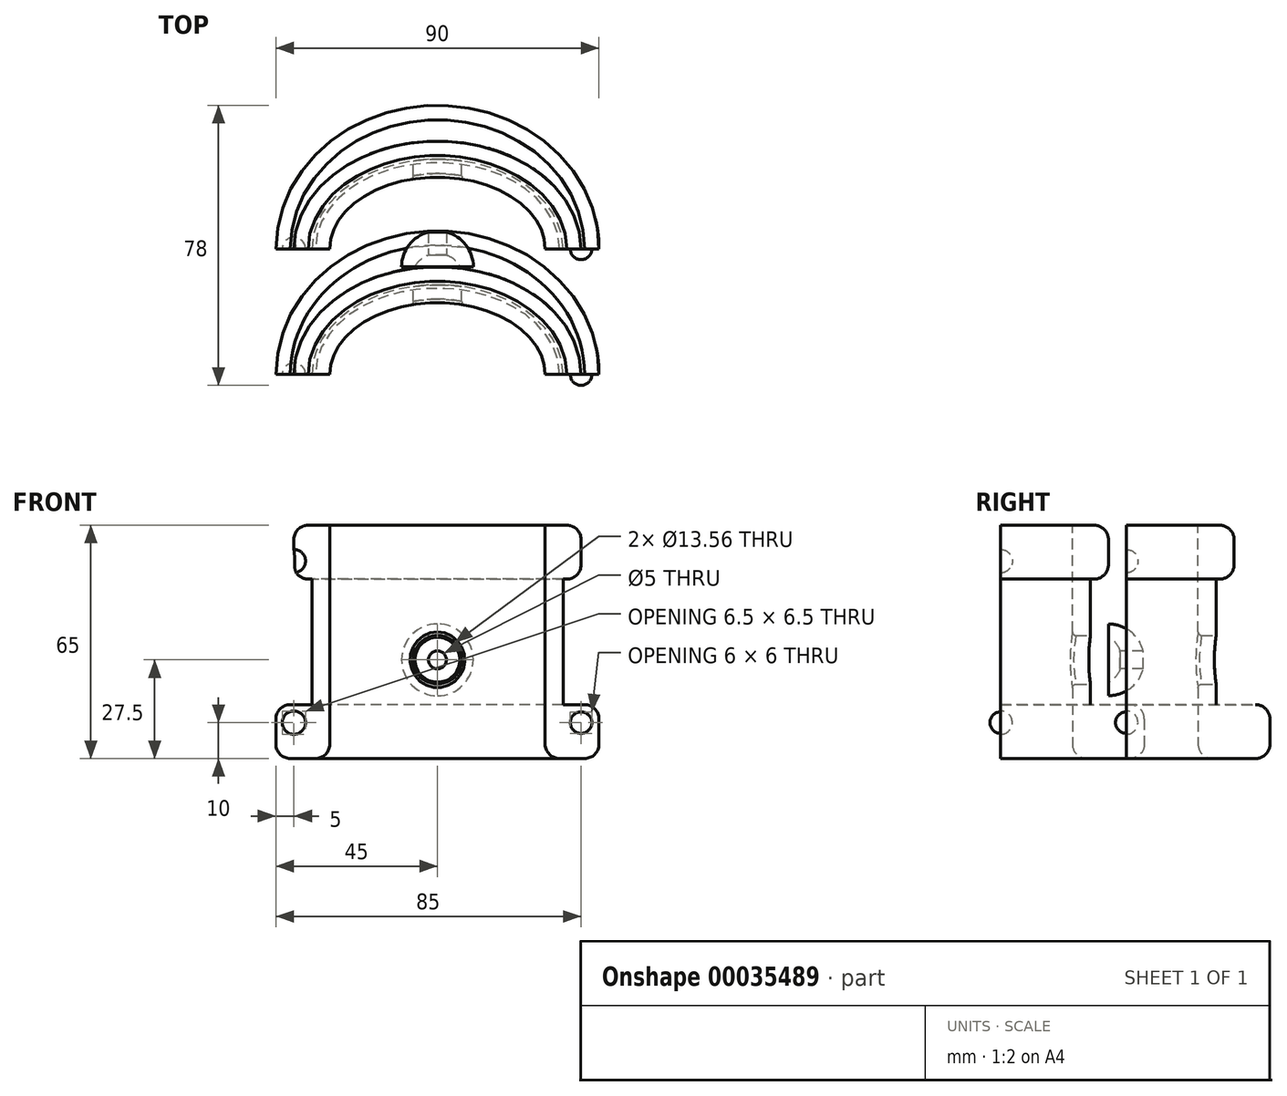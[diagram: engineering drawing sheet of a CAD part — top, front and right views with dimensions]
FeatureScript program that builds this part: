
annotation { "Feature Type Name" : "Feature", "Feature Type Description" : "" }
export const myFeature = defineFeature(function(context is Context, id is Id, definition is map)
    precondition{}
    {
        {
            var Q0;
            Q0=qCreatedBy(makeId("Top.planeOp"),FACE);
            var sketch = newSketch(context, id + "F0", { "sketchPlane" : qUnion([Q0])});
            skEllipse(sketch, "E0", {"center": v(0, 0) * mm, "majorRadius": 45 * mm, "minorRadius": 40 * mm, "majorAxis": v(1, 0)});
            skSolve(sketch);
        }
        {
            var Q0;
            Q0 = qSketchRegion(id + "F0", true);
            extrude(context, id + "F1", {"entities" : qUnion([Q0]), "depth" : 15 * mm});
        }
        {
            var Q0;
            Q0=makeQuery(id+"F1.opExtrude","CAP_FACE",FACE,{"disambiguationData":[OSD([sQuery(id+"F0.wireOp",EDGE,"E0")])],"isStart":false});
            var sketch = newSketch(context, id + "F2", { "sketchPlane" : qUnion([Q0])});
            skEllipse(sketch, "E1", {"center": v(0, 0) * mm, "majorRadius": 35 * mm, "minorRadius": 25 * mm, "majorAxis": v(1, 0)});
            skLineSegment(sketch, "E2", {"start": v(40, 0) * mm, "end": v(45, 0) * mm, "construction": true});
            skLineSegment(sketch, "E3", {"start": v(0, 35) * mm, "end": v(0, 40) * mm, "construction": true});
            skSolve(sketch);
        }
        {
            var Q0;
            Q0 = qSketchRegion(id + "F2", true);
            extrude(context, id + "F3", {"entities" : qUnion([Q0]), "operationType" : NewBodyOperationType.ADD, "depth" : 35 * mm});
        }
        {
            var Q0;
            Q0=makeQuery(id+"F3.opExtrude","CAP_FACE",FACE,{"disambiguationData":[OSD([sQuery(id+"F2.wireOp",EDGE,"E1")])],"isStart":false});
            var sketch = newSketch(context, id + "F4", { "sketchPlane" : qUnion([Q0])});
            skEllipse(sketch, "E4.0", {"center": v(0, 0) * mm, "majorRadius": 40 * mm, "minorRadius": 30 * mm, "majorAxis": v(1, 0)});
            skSolve(sketch);
        }
        {
            var Q0;
            Q0 = qSketchRegion(id + "F4", true);
            extrude(context, id + "F5", {"entities" : qUnion([Q0]), "operationType" : NewBodyOperationType.ADD, "depth" : 15 * mm});
        }
        {
            var Q0;
            Q0=qCreatedBy(makeId("Front.planeOp"),FACE);
            cPlane(context, id + "F6", {"entities" : qUnion([Q0]), "cplaneType" : CPlaneType.OFFSET, "offset" : 20 * mm, "width" : 150 * mm, "height" : 150 * mm});
        }
        {
            var Q0;
            Q0=qCreatedBy(id+"F6.planeOp",FACE);
            var sketch = newSketch(context, id + "F7", { "sketchPlane" : qUnion([Q0])});
            skLineSegment(sketch, "E5", {"start": v(0, 0) * mm, "end": v(0, 27.5) * mm, "construction": true});
            skLineSegment(sketch, "E6", {"start": v(0, 17.5) * mm, "end": v(0, 37.5) * mm});
            skArc(sketch, "E7", {"start": v(0, 17.5) * mm, "mid": v(10, 27.5) * mm, "end": v(0, 37.5) * mm});
            skSolve(sketch);
        }
        {
            var Q0;
            Q0 = qSketchRegion(id + "F7", true);
            var Q1;
            Q1=sQuery(id+"F7.wireOp",EDGE,"E6");
            revolve(context, id + "F8", {"operationType" : NewBodyOperationType.ADD, "entities" : qUnion([Q0]), "axis" : qUnion([Q1]), "revolveType" : RevolveType.ONE_DIRECTION, "oppositeDirection" : true, "angle" : 180 * degree});
        }
        {
            var Q0;
            Q0=qCreatedBy(makeId("Front.planeOp"),FACE);
            cPlane(context, id + "F9", {"entities" : qUnion([Q0]), "cplaneType" : CPlaneType.OFFSET, "offset" : 30 * mm, "oppositeDirection" : true, "width" : 150 * mm, "height" : 150 * mm});
        }
        {
            var Q0;
            Q0=qCreatedBy(id+"F9.planeOp",FACE);
            var sketch = newSketch(context, id + "F10", { "sketchPlane" : qUnion([Q0])});
            skArc(sketch, "E8.0", {"start": v(0, 17.5) * mm, "mid": v(10, 27.5) * mm, "end": v(0, 37.5) * mm});
            skLineSegment(sketch, "E9.0", {"start": v(0, 17.5) * mm, "end": v(0, 37.5) * mm});
            skSolve(sketch);
        }
        {
            var Q0;
            Q0 = qSketchRegion(id + "F10", true);
            var Q1;
            Q1=sQuery(id+"F10.wireOp",EDGE,"E9.0");
            revolve(context, id + "F11", {"operationType" : NewBodyOperationType.ADD, "entities" : qUnion([Q0]), "axis" : qUnion([Q1]), "revolveType" : RevolveType.ONE_DIRECTION, "angle" : 180 * degree});
        }
        {
            var Q0;
            Q0=makeQuery(id+"F5.opExtrude","CAP_FACE",FACE,{"disambiguationData":[OSD([sQuery(id+"F4.wireOp",EDGE,"E4.0")])],"isStart":false});
            var sketch = newSketch(context, id + "F12", { "sketchPlane" : qUnion([Q0])});
            skEllipse(sketch, "E10", {"center": v(0, 0) * mm, "majorRadius": 30 * mm, "minorRadius": 20 * mm, "majorAxis": v(-1, 0)});
            skLineSegment(sketch, "E11", {"start": v(-35, 0) * mm, "end": v(-45, 0) * mm, "construction": true});
            skLineSegment(sketch, "E12", {"start": v(0, -30) * mm, "end": v(0, -40) * mm, "construction": true});
            skSolve(sketch);
        }
        {
            var Q0;
            Q0 = qSketchRegion(id + "F12", true);
            extrude(context, id + "F13", {"entities" : qUnion([Q0]), "operationType" : NewBodyOperationType.REMOVE, "endBound" : BoundingType.THROUGH_ALL, "oppositeDirection" : true, "depth" : 25 * mm});
        }
        {
            var Q0;
            Q0=qCreatedBy(makeId("Front.planeOp"),FACE);
            var sketch = newSketch(context, id + "F14", { "sketchPlane" : qUnion([Q0])});
            skPoint(sketch, "E13.0", {"position": v(0, 27.5) * mm});
            skCircle(sketch, "E14", {"center": v(0, 27.5) * mm, "radius": 2.5 * mm});
            skSolve(sketch);
        }
        {
            var Q0;
            Q0 = qSketchRegion(id + "F14", true);
            extrude(context, id + "F15", {"entities" : qUnion([Q0]), "operationType" : NewBodyOperationType.REMOVE, "endBound" : BoundingType.THROUGH_ALL, "oppositeDirection" : true, "depth" : 25 * mm, "hasSecondDirection" : true, "secondDirectionBound" : SecondDirectionBoundingType.THROUGH_ALL, "secondDirectionOppositeDirection" : false, "secondDirectionDepth" : 25 * mm});
        }
        {
            var Q0;
            Q0=makeQuery(id+"F13.boolean.opBoolean","COPY",EDGE,{"derivedFrom":makeQuery(id+"F13.opExtrude","CAP_EDGE",EDGE,{"disambiguationData":[OSD([sQuery(id+"F12.wireOp",EDGE,"E10")])],"isStart":true})});
            var Q1;
            Q1=makeQuery(id+"F5.opExtrude","CAP_EDGE",EDGE,{"disambiguationData":[OSD([sQuery(id+"F4.wireOp",EDGE,"E4.0")])],"isStart":false});
            var Q2;
            Q2=makeQuery(id+"F1.opExtrude","CAP_EDGE",EDGE,{"disambiguationData":[OSD([sQuery(id+"F0.wireOp",EDGE,"E0")])],"isStart":false});
            var Q3;
            Q3=makeQuery(id+"F1.opExtrude","CAP_EDGE",EDGE,{"disambiguationData":[OSD([sQuery(id+"F0.wireOp",EDGE,"E0")])],"isStart":true});
            var Q4;
            Q4=makeQuery(id+"F13.boolean.opBoolean","INTERSECT",EDGE,{"derivedFrom":[makeQuery(id+"F1.opExtrude","CAP_FACE",FACE,{"disambiguationData":[OSD([sQuery(id+"F0.wireOp",EDGE,"E0")])],"isStart":true}),makeQuery(id+"F13.opExtrude","SWEPT_FACE",FACE,{"disambiguationData":[OSD([sQuery(id+"F12.wireOp",EDGE,"E10")])]})]});
            var Q5;
            Q5=makeQuery(id+"F5.opExtrude","CAP_EDGE",EDGE,{"disambiguationData":[OSD([sQuery(id+"F4.wireOp",EDGE,"E4.0")])],"isStart":true});
            fillet(context, id + "F16", {"entities" : qUnion([Q0, Q1, Q2, Q3, Q4, Q5]), "radius" : 4 * mm, "tangentPropagation" : true, "allowEdgeOverflow" : false});
        }
        {
            var Q0;
            Q0=qCreatedBy(makeId("Right.planeOp"),FACE);
            var sketch = newSketch(context, id + "F17", { "sketchPlane" : qUnion([Q0])});
            skPoint(sketch, "E15.0", {"position": v(-20, 27.5) * mm});
            skLineSegment(sketch, "E16", {"start": v(0, 0) * mm, "end": v(0, 27.5) * mm, "construction": true});
            skLineSegment(sketch, "E17.rect.top", {"start": v(-27.5, 20.72) * mm, "end": v(27.5, 20.72) * mm});
            skPoint(sketch, "E17.rect.middle", {"position": v(0, 27.5) * mm});
            skLineSegment(sketch, "E18", {"start": v(-33.5, 27.5) * mm, "end": v(33.5, 27.5) * mm});
            skArc(sketch, "E19", {"start": v(-33.5, 27.5) * mm, "mid": v(-32.03, 22.76) * mm, "end": v(-27.5, 20.72) * mm});
            skArc(sketch, "E20.MirrorCS", {"start": v(33.5, 27.5) * mm, "mid": v(32.03, 22.76) * mm, "end": v(27.5, 20.72) * mm});
            skSolve(sketch);
        }
        {
            var Q0;
            Q0 = qSketchRegion(id + "F17", true);
            var Q1;
            Q1=sQuery(id+"F17.wireOp",EDGE,"E18");
            revolve(context, id + "F18", {"operationType" : NewBodyOperationType.REMOVE, "entities" : qUnion([Q0]), "axis" : qUnion([Q1]), "revolveType" : RevolveType.FULL, "oppositeDirection" : true});
        }
        {
            var Q0;
            Q0=makeQuery(id+"F3.opExtrude","CAP_EDGE",EDGE,{"disambiguationData":[OSD([sQuery(id+"F2.wireOp",EDGE,"E1")])],"isStart":true});
            var Q1;
            Q1=makeQuery(id+"F3.opExtrude","CAP_EDGE",EDGE,{"disambiguationData":[OSD([sQuery(id+"F2.wireOp",EDGE,"E1")])],"isStart":false});
            var Q2;
            Q2=makeQuery(id+"F18.boolean.opBoolean","INTERSECT",EDGE,{"disambiguationData":[OD(2.0)],"derivedFrom":[makeQuery(id+"F13.boolean.opBoolean","COPY",FACE,{"derivedFrom":makeQuery(id+"F13.opExtrude","SWEPT_FACE",FACE,{"disambiguationData":[OSD([sQuery(id+"F12.wireOp",EDGE,"E10")])]})}),makeQuery(id+"F18.opRevolve","SWEPT_FACE",FACE,{"disambiguationData":[OSD([sQuery(id+"F17.wireOp",EDGE,"E17.rect.top")])]})]});
            var Q3;
            Q3=makeQuery(id+"F18.boolean.opBoolean","INTERSECT",EDGE,{"disambiguationData":[OD(0.0)],"derivedFrom":[makeQuery(id+"F13.boolean.opBoolean","COPY",FACE,{"derivedFrom":makeQuery(id+"F13.opExtrude","SWEPT_FACE",FACE,{"disambiguationData":[OSD([sQuery(id+"F12.wireOp",EDGE,"E10")])]})}),makeQuery(id+"F18.opRevolve","SWEPT_FACE",FACE,{"disambiguationData":[OSD([sQuery(id+"F17.wireOp",EDGE,"E17.rect.top")])]})]});
            fillet(context, id + "F19", {"entities" : qUnion([Q0, Q1, Q2, Q3]), "radius" : 1 * mm, "tangentPropagation" : true, "allowEdgeOverflow" : false});
        }
        {
            var Q0;
            Q0=qCreatedBy(makeId("Top.planeOp"),FACE);
            var sketch = newSketch(context, id + "F20", { "sketchPlane" : qUnion([Q0])});
            skLineSegment(sketch, "E21", {"start": v(50, 0) * mm, "end": v(-50, 0) * mm, "construction": true});
            skLineSegment(sketch, "E22.bottom", {"start": v(50, 0) * mm, "end": v(-50, 0) * mm});
            skLineSegment(sketch, "E22.top", {"start": v(50, -40) * mm, "end": v(-50, -40) * mm});
            skLineSegment(sketch, "E22.left", {"start": v(50, 0) * mm, "end": v(50, -40) * mm});
            skLineSegment(sketch, "E22.right", {"start": v(-50, 0) * mm, "end": v(-50, -40) * mm});
            skSolve(sketch);
        }
        {
            var Q0;
            Q0 = qSketchRegion(id + "F20", true);
            extrude(context, id + "F21", {"entities" : qUnion([Q0]), "operationType" : NewBodyOperationType.REMOVE, "endBound" : BoundingType.THROUGH_ALL, "depth" : 25 * mm});
        }
        {
            var Q0;
            Q0=makeQuery(id+"F21.boolean.opBoolean","COPY",FACE,{"disambiguationData":[OD(1.0)],"derivedFrom":makeQuery(id+"F21.opExtrude","SWEPT_FACE",FACE,{"disambiguationData":[OSD([sQuery(id+"F20.wireOp",EDGE,"E22.bottom")])]})});
            var sketch = newSketch(context, id + "F22", { "sketchPlane" : qUnion([Q0])});
            skLineSegment(sketch, "E23", {"start": v(0, 0) * mm, "end": v(0, 10) * mm, "construction": true});
            skLineSegment(sketch, "E24", {"start": v(0, 10) * mm, "end": v(40, 10) * mm, "construction": true});
            skLineSegment(sketch, "E25", {"start": v(40, 7) * mm, "end": v(40, 13) * mm});
            skArc(sketch, "E26", {"start": v(40, 7) * mm, "mid": v(43, 10) * mm, "end": v(40, 13) * mm});
            skLineSegment(sketch, "E27", {"start": v(35, 32.5) * mm, "end": v(18.77, 32.5) * mm, "construction": true});
            skArc(sketch, "E28.MirrorCS", {"start": v(40, 58) * mm, "mid": v(43, 55) * mm, "end": v(40, 52) * mm});
            skLineSegment(sketch, "E29.MirrorCS", {"start": v(40, 58) * mm, "end": v(40, 52) * mm});
            skSolve(sketch);
        }
        {
            var Q0;
            Q0=makeQuery(id+"F22.imprint","IMPRINT",FACE,{"disambiguationData":[TD([[makeQuery(id+"F22.imprint","IMPRINT",EDGE,{"derivedFrom":sQuery(id+"F22.wireOp",EDGE,"E25")}),-1.0]])]});
            var Q1;
            Q1=makeQuery(id+"F22.imprint","IMPRINT",FACE,{"disambiguationData":[TD([[makeQuery(id+"F22.imprint","IMPRINT",EDGE,{"derivedFrom":sQuery(id+"F22.wireOp",EDGE,"E28.MirrorCS")}),-1.0]])]});
            var Q2;
            Q2=sQuery(id+"F22.wireOp",EDGE,"E25");
            revolve(context, id + "F23", {"operationType" : NewBodyOperationType.ADD, "entities" : qUnion([Q0, Q1]), "axis" : qUnion([Q2]), "revolveType" : RevolveType.FULL});
        }
        {
            var Q0;
            Q0=makeQuery(id+"F21.boolean.opBoolean","COPY",FACE,{"disambiguationData":[OD(0.0)],"derivedFrom":makeQuery(id+"F21.opExtrude","SWEPT_FACE",FACE,{"disambiguationData":[OSD([sQuery(id+"F20.wireOp",EDGE,"E22.bottom")])]})});
            var sketch = newSketch(context, id + "F24", { "sketchPlane" : qUnion([Q0])});
            skLineSegment(sketch, "E30.0", {"start": v(0, 0) * mm, "end": v(0, 10) * mm, "construction": true});
            skArc(sketch, "E31.MirrorCS", {"start": v(-40, 13.25) * mm, "mid": v(-36.75, 10) * mm, "end": v(-40, 6.75) * mm});
            skLineSegment(sketch, "E32", {"start": v(-40, 10) * mm, "end": v(0, 10) * mm, "construction": true});
            skLineSegment(sketch, "E33", {"start": v(-35, 32.5) * mm, "end": v(-16.94, 32.5) * mm, "construction": true});
            skPoint(sketch, "E33.endSnap0", {"position": v(-35, 32.5) * mm});
            skArc(sketch, "E34.MirrorCS", {"start": v(-40, 51.75) * mm, "mid": v(-36.75, 55) * mm, "end": v(-40, 58.25) * mm});
            skLineSegment(sketch, "E35", {"start": v(-40, 6.75) * mm, "end": v(-40, 13.25) * mm});
            skLineSegment(sketch, "E36.MirrorCS", {"start": v(-40, 58.25) * mm, "end": v(-40, 51.75) * mm});
            skSolve(sketch);
        }
        {
            var Q0;
            Q0 = qSketchRegion(id + "F24", true);
            var Q1;
            Q1=sQuery(id+"F24.wireOp",EDGE,"E35");
            revolve(context, id + "F25", {"operationType" : NewBodyOperationType.REMOVE, "entities" : qUnion([Q0]), "axis" : qUnion([Q1]), "revolveType" : RevolveType.FULL, "oppositeDirection" : true});
        }
        {
            var Q0;
            Q0=makeQuery(id+"F1.opExtrude","SWEPT_BODY",BODY,{"disambiguationData":[OSD([sQuery(id+"F0.wireOp",EDGE,"E0")])]});
            transform(context, id + "F26", {"entities" : qUnion([Q0]), "transformType" : TransformType.TRANSLATION_3D, "dx" : 0 * mm, "dy" : 35 * mm, "dz" : 0 * mm, "makeCopy" : true});
        }
    });
